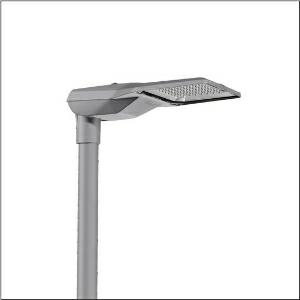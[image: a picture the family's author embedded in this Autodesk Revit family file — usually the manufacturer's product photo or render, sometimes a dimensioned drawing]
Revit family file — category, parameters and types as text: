
# Revit family: streetlight_sl_21_midi___st1_0a_5xe3d33s08lb_350a
name_source: partatom
category: Lighting Fixtures
units: mm (PartAtom-declared; Revit-internal decimal feet)

## family parameters
Cut with Voids When Loaded = No
Host = Face
Light Source = No
Part Type = Normal
Room Calculation Point = No
Round Connector Dimension = Use Diameter
Shared = No

## types (1)
- --- (1 x LED, 14340 lm, 99.6 W, 3000K)
    Apparent Load = 100 VA
    CIE Flux Codes = 37 72 97 100 100
    Color Rendering = 70
    Color Temperature = 3000K
    Default Elevation = 1800 mm
    Description = Streetlight SL 21 midi, mast luminaire, primary light control with lens, of PMMA, primary optical cover: cover, of toughened safety glass, transparent, light distribution: ST1.0a, light emission: direct distribution, primary light characteristic: asymmetric, installation type: side-entry, post-top, LED, High Power LED, rated luminous flux: 14.340lm, luminous efficacy: 144lm/W, light colour: 730, colour temperature: 3000K, control gear: D4i, control: flexible luminous flux parameterisation, time-dependent luminous flux control, constant luminous flux control, overheat protection, pre-setting: logarithmic dimming characteristic, mains connection: 230..240V, AC, 50/60Hz, start of lifetime: 100W, end of service life: 102W, reduction: 46W, luminaire housing, of diecast aluminium, powder-coated, Siteco® metallic grey (DB 702S), corrosivity category C5 mid according to DIN EN ISO 12944, please order mast flange separately, inclination adjustable: 0°, 5°, 10°, 15°, sealing non-destructively replaceable, multi-level sealing system, length: 644mm, width: 335mm, height: 110mm, mast flange for spigot size: 42mm (side-entry): 5XC10008XM4, 60/48mm (side-entry/post-top): 5XC10108XM2, 76/60mm (side-entry/post-top): 5XC10108XM1, mounting height: 4..8m, Smart Interface above, protection rating (complete): IP66, insulation class (complete): insulation class II (safety insulation), certification: CE, ENEC, ENEC+, VDE, impact resistance: IK10, permissible operating ambient temperature for outdoor applications: -40..+50°C, standard-compliant lighting for roads and squares, packaging unit: 1 piece

Light Distribution: ST1.0a
    Height = 111 mm
    Lamp = 1 x LED
    Lamp Light Flux = 14340 lm
    Lamp Power = 99.6 W
    Lamp count = 1
    Length = 644 mm
    Luminous efficacy = 144 lm/W
    Manufacturer = Siteco
    ModVariant = No
    Model = 5XE3D33S08LB
    Number of Poles = 1
    OnlyDefault = Yes
    Power Factor = 1
    Product Name = Streetlight SL 21 midi | ST1.0a
    Product group = mast luminaire | pylon top
    ProductGroupID = 6100
    Protection Class = Protection class II
    Protection Degree = IP 66
    RLX_Detail_Level = 1
    RLX_Emergency_Light_Flux = 0 lm
    RLX_Emergency_Type = 0
    RLX_Emergency_Type_DB = No
    RlxData = <blob elided: 26761 chars, md5=26857ad3>
    Socket = socket
    Standby Power = 0 W
    System Light Flux = 14340 lm
    System Power = 100 W
    Type Comments = factory setting: luminous flux: 100 % | dim-lin: 254 | 1020 mA
    Type Image = l_1004302.jpg
    URL = http://relux.com
    VarID = @adj_031933
    Voltage = 0 V
    Weight = 0.00 kg
    Width = 336 mm

## geometry (parser evidence)
native form markers: Blend x4, Sweep x11
no freeform markers — native parametric forms only
